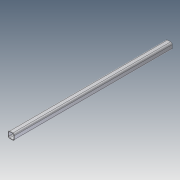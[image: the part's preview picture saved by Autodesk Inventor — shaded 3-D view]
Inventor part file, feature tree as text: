
AUTODESK INVENTOR PART (.ipt)
format: ipt  version: unknown  size: 179,200 bytes
history: native  units: in
note: dims shown in document units (in); Inventor stores cm internally (conversion verified against a paired STEP export)
features: extrude x1, sketch x1
ambient origin geometry x8: Origin, YZ Plane, XZ Plane, XY Plane, X Axis, Y Axis, Z Axis, Center Point
bodies: Solid1 (feature_tree)
feature tree (2):
  extrude  "Extrusion1"  Depth=0.375in
  sketch  "Sketch1"  dims[d0=1.5in d1=0.375in d2=0.125in d3=37.0in d4=0.0in]
